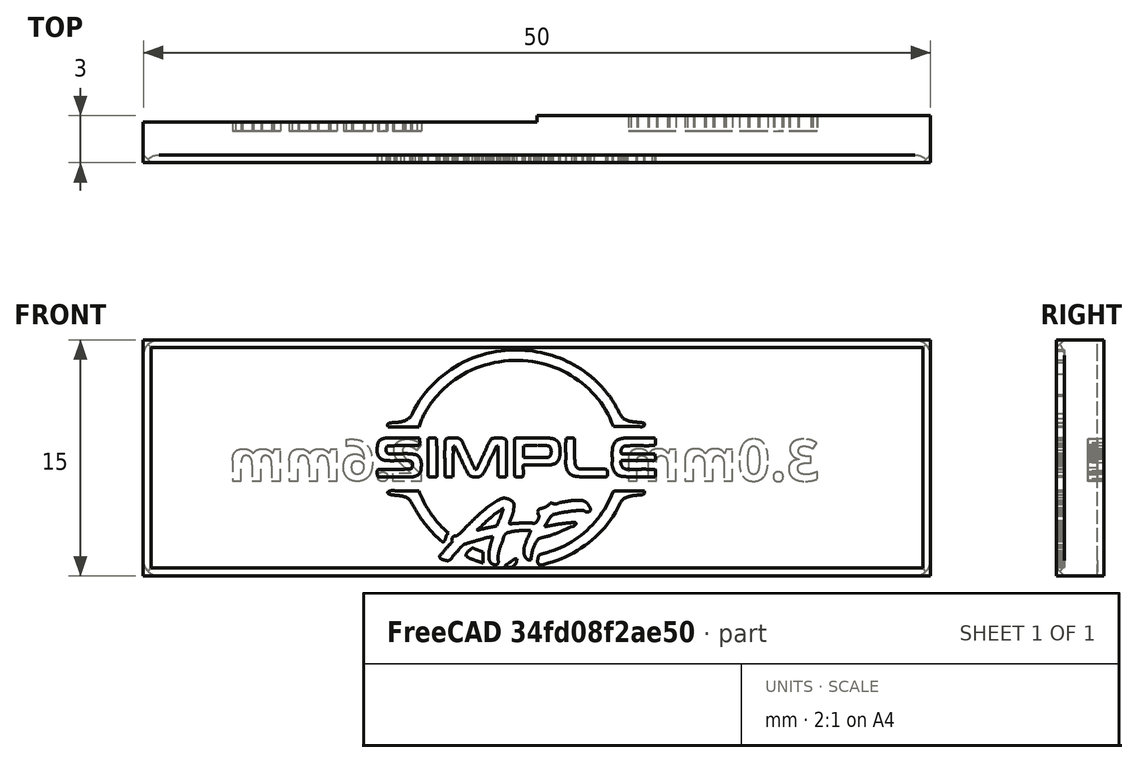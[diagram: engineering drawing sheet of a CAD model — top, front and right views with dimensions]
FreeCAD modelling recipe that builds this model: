
FCSTD DOCUMENT  (FreeCAD 26.3R20260630 (Git shallow))
Label: goldilocks
License: All rights reserved
LicenseURL: http://en.wikipedia.org/wiki/All_rights_reserved
objects: Sketcher::SketchObject×4, App::Point×2, PartDesign::Pad×2, PartDesign::Pocket×2, PartDesign::Body×2, PartDesign::Chamfer×1, PartDesign::Fillet×1
note: 28 computed .brp shape members not serialized (recipe doc carries the construction recipe); baked Part::Feature solids carry a one-line shape summary decoded from their .brp

FEATURE [App::Point] Origin001
  Role = Origin
FEATURE [Sketcher::SketchObject] Sketch
  ArcFitTolerance = 1e-06
  AttachmentSupport = -> [XY_Plane]
  ExternalTypes = [0]
  FullyConstrained = false
  MakeInternals = false
  MapMode = 5
  sketch-geometry (6):
    g0: LineSegment StartX=-28.082 StartY=2.6 StartZ=0 EndX=-3.08196 EndY=2.6 EndZ=0
    g1: LineSegment StartX=-3.08196 StartY=2.6 StartZ=0 EndX=-3.08196 EndY=3 EndZ=0
    g2: LineSegment StartX=-3.08196 StartY=3 StartZ=0 EndX=21.918 EndY=3 EndZ=0
    g3: LineSegment StartX=21.918 StartY=3 StartZ=0 EndX=21.918 EndY=0 EndZ=0
    g4: LineSegment StartX=21.918 StartY=0 StartZ=0 EndX=-28.082 EndY=0 EndZ=0
    g5: LineSegment StartX=-28.082 StartY=0 StartZ=0 EndX=-28.082 EndY=2.6 EndZ=0
  constraints (17):
    c: Horizontal(g0)
    c: Coincident(g0,g1)
    c: Vertical(g1)
    c: Coincident(g1,g2)
    c: Horizontal(g2)
    c: Coincident(g2,g3)
    c: PointOnObject(g3,g-1)
    c: Vertical(g3)
    c: Coincident(g3,g4)
    c: PointOnObject(g4,g-1)
    c: Coincident(g4,g5)
    c: Coincident(g5,g0)
    c: Vertical(g5)
    c: DistanceY(g5,g5) = 2.6
    c: DistanceY(g3,g3) = 3
    c: DistanceX(g4,g4) = 50
    c: DistanceX(g0,g0) = 25
FEATURE [PartDesign::Pad] Pad
  Direction = (0,0,1)
  FuzzyTolerance = 0
  Length = 15
  Length2 = 10
  Profile = -> Sketch
  ReferenceAxis = -> Sketch [N_Axis]
  SideType = 0
  Suppressed = false
  Type = 0
  Type2 = 0
FEATURE [Sketcher::SketchObject] Sketch001
  ArcFitTolerance = 1e-06
  AttachmentOffset = pos=(1,3.5,0) rot=(0,0,1;0rad)
  AttachmentSupport = -> [Pad]
  ExternalTypes = [0]
  FullyConstrained = false
  MakeInternals = true
  MapMode = 5
  Placement = pos=(1,8e-16,3.5) rot=(1,0,0;1.5708rad)
  sketch-geometry (160):
    g0: BSplineCurve PolesCount=4 KnotsCount=2 Degree=3 IsPeriodic=0
    g1: BSplineCurve PolesCount=4 KnotsCount=2 Degree=3 IsPeriodic=0
    g2: BSplineCurve PolesCount=4 KnotsCount=2 Degree=3 IsPeriodic=0
    g3: BSplineCurve PolesCount=4 KnotsCount=2 Degree=3 IsPeriodic=0
    g4: BSplineCurve PolesCount=4 KnotsCount=2 Degree=3 IsPeriodic=0
    g5: BSplineCurve PolesCount=4 KnotsCount=2 Degree=3 IsPeriodic=0
    g6: BSplineCurve PolesCount=4 KnotsCount=2 Degree=3 IsPeriodic=0
    g7: BSplineCurve PolesCount=4 KnotsCount=2 Degree=3 IsPeriodic=0
    g8: BSplineCurve PolesCount=4 KnotsCount=2 Degree=3 IsPeriodic=0
    g9: BSplineCurve PolesCount=4 KnotsCount=2 Degree=3 IsPeriodic=0
    g10: BSplineCurve PolesCount=4 KnotsCount=2 Degree=3 IsPeriodic=0
    g11: BSplineCurve PolesCount=4 KnotsCount=2 Degree=3 IsPeriodic=0
    g12: BSplineCurve PolesCount=4 KnotsCount=2 Degree=3 IsPeriodic=0
    g13: BSplineCurve PolesCount=4 KnotsCount=2 Degree=3 IsPeriodic=0
    g14: BSplineCurve PolesCount=4 KnotsCount=2 Degree=3 IsPeriodic=0
    g15: BSplineCurve PolesCount=4 KnotsCount=2 Degree=3 IsPeriodic=0
    g16: BSplineCurve PolesCount=4 KnotsCount=2 Degree=3 IsPeriodic=0
    g17: BSplineCurve PolesCount=4 KnotsCount=2 Degree=3 IsPeriodic=0
    g18: BSplineCurve PolesCount=4 KnotsCount=2 Degree=3 IsPeriodic=0
    g19: BSplineCurve PolesCount=4 KnotsCount=2 Degree=3 IsPeriodic=0
    g20: BSplineCurve PolesCount=4 KnotsCount=2 Degree=3 IsPeriodic=0
    g21: BSplineCurve PolesCount=4 KnotsCount=2 Degree=3 IsPeriodic=0
    g22: BSplineCurve PolesCount=4 KnotsCount=2 Degree=3 IsPeriodic=0
    g23: BSplineCurve PolesCount=4 KnotsCount=2 Degree=3 IsPeriodic=0
    g24: BSplineCurve PolesCount=4 KnotsCount=2 Degree=3 IsPeriodic=0
    g25: BSplineCurve PolesCount=4 KnotsCount=2 Degree=3 IsPeriodic=0
    g26: BSplineCurve PolesCount=4 KnotsCount=2 Degree=3 IsPeriodic=0
    g27: BSplineCurve PolesCount=4 KnotsCount=2 Degree=3 IsPeriodic=0
    g28: BSplineCurve PolesCount=4 KnotsCount=2 Degree=3 IsPeriodic=0
    g29: BSplineCurve PolesCount=4 KnotsCount=2 Degree=3 IsPeriodic=0
    g30: BSplineCurve PolesCount=4 KnotsCount=2 Degree=3 IsPeriodic=0
    g31: BSplineCurve PolesCount=4 KnotsCount=2 Degree=3 IsPeriodic=0
    g32: BSplineCurve PolesCount=4 KnotsCount=2 Degree=3 IsPeriodic=0
    g33: BSplineCurve PolesCount=4 KnotsCount=2 Degree=3 IsPeriodic=0
    g34: BSplineCurve PolesCount=4 KnotsCount=2 Degree=3 IsPeriodic=0
    g35: BSplineCurve PolesCount=4 KnotsCount=2 Degree=3 IsPeriodic=0
    g36: BSplineCurve PolesCount=4 KnotsCount=2 Degree=3 IsPeriodic=0
    g37: BSplineCurve PolesCount=4 KnotsCount=2 Degree=3 IsPeriodic=0
    g38: BSplineCurve PolesCount=4 KnotsCount=2 Degree=3 IsPeriodic=0
    g39: BSplineCurve PolesCount=4 KnotsCount=2 Degree=3 IsPeriodic=0
    g40: BSplineCurve PolesCount=4 KnotsCount=2 Degree=3 IsPeriodic=0
    g41: BSplineCurve PolesCount=4 KnotsCount=2 Degree=3 IsPeriodic=0
    g42: BSplineCurve PolesCount=4 KnotsCount=2 Degree=3 IsPeriodic=0
    g43: BSplineCurve PolesCount=4 KnotsCount=2 Degree=3 IsPeriodic=0
    g44: BSplineCurve PolesCount=4 KnotsCount=2 Degree=3 IsPeriodic=0
    g45: BSplineCurve PolesCount=4 KnotsCount=2 Degree=3 IsPeriodic=0
    g46: BSplineCurve PolesCount=4 KnotsCount=2 Degree=3 IsPeriodic=0
    g47: BSplineCurve PolesCount=4 KnotsCount=2 Degree=3 IsPeriodic=0
    g48: BSplineCurve PolesCount=4 KnotsCount=2 Degree=3 IsPeriodic=0
    g49: BSplineCurve PolesCount=4 KnotsCount=2 Degree=3 IsPeriodic=0
    g50: BSplineCurve PolesCount=4 KnotsCount=2 Degree=3 IsPeriodic=0
    g51: BSplineCurve PolesCount=4 KnotsCount=2 Degree=3 IsPeriodic=0
    g52: BSplineCurve PolesCount=4 KnotsCount=2 Degree=3 IsPeriodic=0
    g53: BSplineCurve PolesCount=4 KnotsCount=2 Degree=3 IsPeriodic=0
    g54: BSplineCurve PolesCount=4 KnotsCount=2 Degree=3 IsPeriodic=0
    g55: BSplineCurve PolesCount=4 KnotsCount=2 Degree=3 IsPeriodic=0
    g56: BSplineCurve PolesCount=4 KnotsCount=2 Degree=3 IsPeriodic=0
    g57: BSplineCurve PolesCount=4 KnotsCount=2 Degree=3 IsPeriodic=0
    g58: BSplineCurve PolesCount=4 KnotsCount=2 Degree=3 IsPeriodic=0
    g59: BSplineCurve PolesCount=4 KnotsCount=2 Degree=3 IsPeriodic=0
    g60: BSplineCurve PolesCount=4 KnotsCount=2 Degree=3 IsPeriodic=0
    g61: BSplineCurve PolesCount=4 KnotsCount=2 Degree=3 IsPeriodic=0
    g62: BSplineCurve PolesCount=4 KnotsCount=2 Degree=3 IsPeriodic=0
    g63: BSplineCurve PolesCount=4 KnotsCount=2 Degree=3 IsPeriodic=0
    g64: BSplineCurve PolesCount=4 KnotsCount=2 Degree=3 IsPeriodic=0
    g65: BSplineCurve PolesCount=4 KnotsCount=2 Degree=3 IsPeriodic=0
    g66: BSplineCurve PolesCount=4 KnotsCount=2 Degree=3 IsPeriodic=0
    g67: BSplineCurve PolesCount=4 KnotsCount=2 Degree=3 IsPeriodic=0
    g68: BSplineCurve PolesCount=4 KnotsCount=2 Degree=3 IsPeriodic=0
    g69: BSplineCurve PolesCount=4 KnotsCount=2 Degree=3 IsPeriodic=0
    g70: BSplineCurve PolesCount=4 KnotsCount=2 Degree=3 IsPeriodic=0
    g71: BSplineCurve PolesCount=4 KnotsCount=2 Degree=3 IsPeriodic=0
    g72: BSplineCurve PolesCount=4 KnotsCount=2 Degree=3 IsPeriodic=0
    g73: BSplineCurve PolesCount=4 KnotsCount=2 Degree=3 IsPeriodic=0
    g74: BSplineCurve PolesCount=4 KnotsCount=2 Degree=3 IsPeriodic=0
    g75: BSplineCurve PolesCount=4 KnotsCount=2 Degree=3 IsPeriodic=0
    g76: BSplineCurve PolesCount=4 KnotsCount=2 Degree=3 IsPeriodic=0
    g77: BSplineCurve PolesCount=4 KnotsCount=2 Degree=3 IsPeriodic=0
    g78: BSplineCurve PolesCount=4 KnotsCount=2 Degree=3 IsPeriodic=0
    g79: BSplineCurve PolesCount=4 KnotsCount=2 Degree=3 IsPeriodic=0
    g80: BSplineCurve PolesCount=4 KnotsCount=2 Degree=3 IsPeriodic=0
    g81: BSplineCurve PolesCount=4 KnotsCount=2 Degree=3 IsPeriodic=0
    g82: BSplineCurve PolesCount=4 KnotsCount=2 Degree=3 IsPeriodic=0
    g83: BSplineCurve PolesCount=4 KnotsCount=2 Degree=3 IsPeriodic=0
    g84: BSplineCurve PolesCount=4 KnotsCount=2 Degree=3 IsPeriodic=0
    g85: BSplineCurve PolesCount=4 KnotsCount=2 Degree=3 IsPeriodic=0
    g86: BSplineCurve PolesCount=4 KnotsCount=2 Degree=3 IsPeriodic=0
    g87: BSplineCurve PolesCount=4 KnotsCount=2 Degree=3 IsPeriodic=0
    g88: BSplineCurve PolesCount=4 KnotsCount=2 Degree=3 IsPeriodic=0
    g89: BSplineCurve PolesCount=4 KnotsCount=2 Degree=3 IsPeriodic=0
    g90: BSplineCurve PolesCount=4 KnotsCount=2 Degree=3 IsPeriodic=0
    g91: BSplineCurve PolesCount=4 KnotsCount=2 Degree=3 IsPeriodic=0
    g92: BSplineCurve PolesCount=4 KnotsCount=2 Degree=3 IsPeriodic=0
    g93: BSplineCurve PolesCount=4 KnotsCount=2 Degree=3 IsPeriodic=0
    g94: BSplineCurve PolesCount=4 KnotsCount=2 Degree=3 IsPeriodic=0
    g95: BSplineCurve PolesCount=4 KnotsCount=2 Degree=3 IsPeriodic=0
    g96: BSplineCurve PolesCount=4 KnotsCount=2 Degree=3 IsPeriodic=0
    g97: BSplineCurve PolesCount=4 KnotsCount=2 Degree=3 IsPeriodic=0
    g98: BSplineCurve PolesCount=4 KnotsCount=2 Degree=3 IsPeriodic=0
    g99: BSplineCurve PolesCount=4 KnotsCount=2 Degree=3 IsPeriodic=0
    g100: BSplineCurve PolesCount=4 KnotsCount=2 Degree=3 IsPeriodic=0
    g101: BSplineCurve PolesCount=4 KnotsCount=2 Degree=3 IsPeriodic=0
    g102: BSplineCurve PolesCount=4 KnotsCount=2 Degree=3 IsPeriodic=0
    g103: BSplineCurve PolesCount=4 KnotsCount=2 Degree=3 IsPeriodic=0
    g104: BSplineCurve PolesCount=4 KnotsCount=2 Degree=3 IsPeriodic=0
    g105: BSplineCurve PolesCount=2 KnotsCount=2 Degree=1 IsPeriodic=0
    g106: BSplineCurve PolesCount=4 KnotsCount=2 Degree=3 IsPeriodic=0
    g107: BSplineCurve PolesCount=4 KnotsCount=2 Degree=3 IsPeriodic=0
    g108: BSplineCurve PolesCount=4 KnotsCount=2 Degree=3 IsPeriodic=0
    g109: BSplineCurve PolesCount=4 KnotsCount=2 Degree=3 IsPeriodic=0
    g110: BSplineCurve PolesCount=4 KnotsCount=2 Degree=3 IsPeriodic=0
    g111: BSplineCurve PolesCount=4 KnotsCount=2 Degree=3 IsPeriodic=0
    g112: BSplineCurve PolesCount=4 KnotsCount=2 Degree=3 IsPeriodic=0
    g113: BSplineCurve PolesCount=4 KnotsCount=2 Degree=3 IsPeriodic=0
    g114: BSplineCurve PolesCount=4 KnotsCount=2 Degree=3 IsPeriodic=0
    g115: BSplineCurve PolesCount=4 KnotsCount=2 Degree=3 IsPeriodic=0
    g116: BSplineCurve PolesCount=4 KnotsCount=2 Degree=3 IsPeriodic=0
    g117: BSplineCurve PolesCount=4 KnotsCount=2 Degree=3 IsPeriodic=0
    g118: BSplineCurve PolesCount=4 KnotsCount=2 Degree=3 IsPeriodic=0
    g119: BSplineCurve PolesCount=4 KnotsCount=2 Degree=3 IsPeriodic=0
    g120: BSplineCurve PolesCount=4 KnotsCount=2 Degree=3 IsPeriodic=0
    g121: BSplineCurve PolesCount=4 KnotsCount=2 Degree=3 IsPeriodic=0
    g122: BSplineCurve PolesCount=4 KnotsCount=2 Degree=3 IsPeriodic=0
    g123: BSplineCurve PolesCount=4 KnotsCount=2 Degree=3 IsPeriodic=0
    g124: BSplineCurve PolesCount=4 KnotsCount=2 Degree=3 IsPeriodic=0
    g125: BSplineCurve PolesCount=4 KnotsCount=2 Degree=3 IsPeriodic=0
    g126: BSplineCurve PolesCount=4 KnotsCount=2 Degree=3 IsPeriodic=0
    g127: BSplineCurve PolesCount=4 KnotsCount=2 Degree=3 IsPeriodic=0
    g128: BSplineCurve PolesCount=4 KnotsCount=2 Degree=3 IsPeriodic=0
    g129: BSplineCurve PolesCount=4 KnotsCount=2 Degree=3 IsPeriodic=0
    g130: BSplineCurve PolesCount=4 KnotsCount=2 Degree=3 IsPeriodic=0
    g131: BSplineCurve PolesCount=4 KnotsCount=2 Degree=3 IsPeriodic=0
    g132: BSplineCurve PolesCount=4 KnotsCount=2 Degree=3 IsPeriodic=0
    g133: BSplineCurve PolesCount=4 KnotsCount=2 Degree=3 IsPeriodic=0
    g134: BSplineCurve PolesCount=4 KnotsCount=2 Degree=3 IsPeriodic=0
    g135: BSplineCurve PolesCount=4 KnotsCount=2 Degree=3 IsPeriodic=0
    g136: BSplineCurve PolesCount=4 KnotsCount=2 Degree=3 IsPeriodic=0
    g137: BSplineCurve PolesCount=4 KnotsCount=2 Degree=3 IsPeriodic=0
    g138: BSplineCurve PolesCount=4 KnotsCount=2 Degree=3 IsPeriodic=0
    g139: BSplineCurve PolesCount=4 KnotsCount=2 Degree=3 IsPeriodic=0
    g140: BSplineCurve PolesCount=4 KnotsCount=2 Degree=3 IsPeriodic=0
    g141: BSplineCurve PolesCount=4 KnotsCount=2 Degree=3 IsPeriodic=0
    g142: BSplineCurve PolesCount=4 KnotsCount=2 Degree=3 IsPeriodic=0
    g143: BSplineCurve PolesCount=4 KnotsCount=2 Degree=3 IsPeriodic=0
    g144: BSplineCurve PolesCount=4 KnotsCount=2 Degree=3 IsPeriodic=0
    g145: BSplineCurve PolesCount=4 KnotsCount=2 Degree=3 IsPeriodic=0
    g146: BSplineCurve PolesCount=4 KnotsCount=2 Degree=3 IsPeriodic=0
    g147: BSplineCurve PolesCount=4 KnotsCount=2 Degree=3 IsPeriodic=0
    g148: BSplineCurve PolesCount=4 KnotsCount=2 Degree=3 IsPeriodic=0
    g149: BSplineCurve PolesCount=4 KnotsCount=2 Degree=3 IsPeriodic=0
    g150: BSplineCurve PolesCount=4 KnotsCount=2 Degree=3 IsPeriodic=0
    g151: BSplineCurve PolesCount=4 KnotsCount=2 Degree=3 IsPeriodic=0
    g152: BSplineCurve PolesCount=4 KnotsCount=2 Degree=3 IsPeriodic=0
    g153: BSplineCurve PolesCount=4 KnotsCount=2 Degree=3 IsPeriodic=0
    g154: BSplineCurve PolesCount=4 KnotsCount=2 Degree=3 IsPeriodic=0
    g155: BSplineCurve PolesCount=4 KnotsCount=2 Degree=3 IsPeriodic=0
    g156: BSplineCurve PolesCount=4 KnotsCount=2 Degree=3 IsPeriodic=0
    g157: BSplineCurve PolesCount=4 KnotsCount=2 Degree=3 IsPeriodic=0
    g158: BSplineCurve PolesCount=4 KnotsCount=2 Degree=3 IsPeriodic=0
    g159: BSplineCurve PolesCount=4 KnotsCount=2 Degree=3 IsPeriodic=0
  constraints (160):
    c: Coincident(g117,g118)
    c: Coincident(g118,g119)
    c: Coincident(g108,g109)
    c: Coincident(g107,g108)
    c: Coincident(g112,g113)
    c: Coincident(g7,g8)
    c: Coincident(g156,g157)
    c: Coincident(g113,g114)
    c: Coincident(g8,g9)
    c: Coincident(g157,g158)
    c: Coincident(g109,g110)
    c: Coincident(g116,g117)
    c: Coincident(g106,g107)
    c: Coincident(g155,g156)
    c: Coincident(g119,g120)
    c: Coincident(g106,g120)
    c: Coincident(g9,g10)
    c: Coincident(g114,g115)
    c: Coincident(g158,g159)
    c: Coincident(g6,g7)
    c: Coincident(g111,g112)
    c: Coincident(g110,g111)
    c: Coincident(g115,g116)
    c: Coincident(g102,g103)
    c: Coincident(g101,g102)
    c: Coincident(g101,g105)
    c: Coincident(g154,g155)
    c: Coincident(g103,g104)
    c: Coincident(g104,g105)
    c: Coincident(g5,g6)
    c: Coincident(g61,g62)
    c: Coincident(g153,g154)
    c: Coincident(g94,g95)
    c: Coincident(g95,g96)
    c: Coincident(g62,g63)
    c: Coincident(g153,g159)
    c: Coincident(g93,g94)
    c: Coincident(g60,g61)
    c: Coincident(g92,g93)
    c: Coincident(g91,g92)
    c: Coincident(g63,g64)
    c: Coincident(g59,g60)
    c: Coincident(g96,g97)
    c: Coincident(g64,g65)
    c: Coincident(g65,g66)
    c: Coincident(g143,g144)
    c: Coincident(g97,g98)
    c: Coincident(g58,g59)
    c: Coincident(g90,g91)
    c: Coincident(g141,g144)
    c: Coincident(g98,g99)
    c: Coincident(g125,g126)
    c: Coincident(g121,g126)
    c: Coincident(g99,g100)
    c: Coincident(g89,g90)
    c: Coincident(g141,g142)
    c: Coincident(g82,g100)
    c: Coincident(g142,g143)
    c: Coincident(g66,g67)
    c: Coincident(g124,g125)
    c: Coincident(g69,g70)
    c: Coincident(g68,g69)
    c: Coincident(g82,g83)
    c: Coincident(g67,g68)
    c: Coincident(g88,g89)
    c: Coincident(g123,g124)
    c: Coincident(g121,g122)
    c: Coincident(g87,g88)
    c: Coincident(g86,g87)
    c: Coincident(g70,g71)
    c: Coincident(g57,g58)
    c: Coincident(g71,g72)
    c: Coincident(g10,g11)
    c: Coincident(g31,g72)
    c: Coincident(g122,g123)
    c: Coincident(g83,g84)
    c: Coincident(g84,g85)
    c: Coincident(g85,g86)
    c: Coincident(g27,g28)
    c: Coincident(g28,g29)
    c: Coincident(g31,g32)
    c: Coincident(g53,g54)
    c: Coincident(g56,g57)
    c: Coincident(g54,g55)
    c: Coincident(g52,g53)
    c: Coincident(g55,g56)
    c: Coincident(g78,g79)
    c: Coincident(g77,g78)
    c: Coincident(g27,g30)
    c: Coincident(g29,g30)
    c: Coincident(g76,g77)
    c: Coincident(g75,g76)
    c: Coincident(g128,g129)
    c: Coincident(g127,g128)
    c: Coincident(g33,g34)
    c: Coincident(g34,g35)
    c: Coincident(g79,g80)
    c: Coincident(g32,g33)
    c: Coincident(g35,g36)
    c: Coincident(g51,g52)
    c: Coincident(g127,g131)
    c: Coincident(g4,g5)
    c: Coincident(g36,g37)
    c: Coincident(g145,g152)
    c: Coincident(g50,g51)
    c: Coincident(g74,g75)
    c: Coincident(g151,g152)
    c: Coincident(g49,g50)
    c: Coincident(g41,g42)
    c: Coincident(g129,g130)
    c: Coincident(g130,g131)
    c: Coincident(g145,g146)
    c: Coincident(g48,g49)
    c: Coincident(g42,g43)
    c: Coincident(g80,g81)
    c: Coincident(g37,g38)
    c: Coincident(g73,g81)
    c: Coincident(g73,g74)
    c: Coincident(g47,g48)
    c: Coincident(g135,g136)
    c: Coincident(g136,g137)
    c: Coincident(g38,g39)
    c: Coincident(g39,g40)
    c: Coincident(g40,g41)
    c: Coincident(g134,g135)
    c: Coincident(g137,g138)
    c: Coincident(g138,g139)
    c: Coincident(g46,g47)
    c: Coincident(g43,g44)
    c: Coincident(g11,g12)
    c: Coincident(g45,g46)
    c: Coincident(g44,g45)
    c: Coincident(g139,g140)
    c: Coincident(g132,g140)
    c: Coincident(g133,g134)
    c: Coincident(g132,g133)
    c: Coincident(g0,g12)
    c: Coincident(g24,g25)
    c: Coincident(g146,g147)
    c: Coincident(g3,g4)
    c: Coincident(g25,g26)
    c: Coincident(g150,g151)
    c: Coincident(g19,g20)
    c: Coincident(g16,g17)
    c: Coincident(g23,g24)
    c: Coincident(g0,g1)
    c: Coincident(g15,g16)
    c: Coincident(g13,g26)
    c: Coincident(g147,g148)
    c: Coincident(g20,g21)
    c: Coincident(g2,g3)
    c: Coincident(g149,g150)
    c: Coincident(g1,g2)
    c: Coincident(g148,g149)
    c: Coincident(g18,g19)
    c: Coincident(g22,g23)
    c: Coincident(g14,g15)
    c: Coincident(g17,g18)
    c: Coincident(g21,g22)
    c: Coincident(g13,g14)
FEATURE [PartDesign::Pocket] Pocket
  BaseFeature = -> Pad
  Direction = (0,1,-2e-16)
  FuzzyTolerance = 0
  Length = 0.5
  Length2 = 5
  Profile = -> Sketch001
  ReferenceAxis = -> Sketch001 [N_Axis]
  Refine = true
  SideType = 0
  Suppressed = false
  Type = 0
  Type2 = 0
FEATURE [PartDesign::Chamfer] Chamfer
  Angle = 45
  Base = -> Pocket [Edge13,Edge16,Edge17,Edge5]
  BaseFeature = -> Pocket
  ChamferType = 0
  FlipDirection = false
  FuzzyTolerance = 0
  Refine = true
  Size = 0.5
  Size2 = 1
  SupportTransform = false
  Suppressed = false
  UseAllEdges = false
FEATURE [PartDesign::Fillet] Fillet
  Base = -> Chamfer [Edge5,Edge1,Edge4,Edge15]
  BaseFeature = -> Chamfer
  FuzzyTolerance = 0
  Radius = 1
  Refine = true
  SupportTransform = false
  Suppressed = false
  UseAllEdges = false
FEATURE [Sketcher::SketchObject] Sketch002
  ArcFitTolerance = 1e-06
  AttachmentSupport = -> [Fillet]
  ExternalTypes = [0]
  FullyConstrained = false
  MakeInternals = true
  MapMode = 5
  Placement = pos=(0,3,0) rot=(0,0.707107,0.707107;3.14159rad)
  sketch-geometry (222):
    g0: LineSegment [constr] StartX=-14.7202 StartY=6 StartZ=0 EndX=-2.72016 EndY=6 EndZ=0
    g1: LineSegment [constr] StartX=10.4105 StartY=6 StartZ=0 EndX=22.4105 EndY=6 EndZ=0
    g2: BSplineCurve PolesCount=3 KnotsCount=2 Degree=2 IsPeriodic=0
    g3: BSplineCurve PolesCount=3 KnotsCount=2 Degree=2 IsPeriodic=0
    g4: LineSegment StartX=-13.5529 StartY=7.4247 StartZ=0 EndX=-13.5529 EndY=7.41397 EndZ=0
    g5: BSplineCurve PolesCount=3 KnotsCount=2 Degree=2 IsPeriodic=0
    g6: BSplineCurve PolesCount=3 KnotsCount=2 Degree=2 IsPeriodic=0
    g7: BSplineCurve PolesCount=3 KnotsCount=2 Degree=2 IsPeriodic=0
    g8: BSplineCurve PolesCount=3 KnotsCount=2 Degree=2 IsPeriodic=0
    g9: BSplineCurve PolesCount=3 KnotsCount=2 Degree=2 IsPeriodic=0
    g10: LineSegment StartX=-14.7202 StartY=6.15373 StartZ=0 EndX=-14.7202 EndY=6.62386 EndZ=0
    g11: BSplineCurve PolesCount=3 KnotsCount=2 Degree=2 IsPeriodic=0
    g12: BSplineCurve PolesCount=3 KnotsCount=2 Degree=2 IsPeriodic=0
    g13: BSplineCurve PolesCount=3 KnotsCount=2 Degree=2 IsPeriodic=0
    g14: BSplineCurve PolesCount=3 KnotsCount=2 Degree=2 IsPeriodic=0
    g15: BSplineCurve PolesCount=3 KnotsCount=2 Degree=2 IsPeriodic=0
    g16: BSplineCurve PolesCount=3 KnotsCount=2 Degree=2 IsPeriodic=0
    g17: LineSegment StartX=-14.1195 StartY=7.1798 StartZ=0 EndX=-14.318 EndY=7.1798 EndZ=0
    g18: LineSegment StartX=-14.318 StartY=7.1798 StartZ=0 EndX=-14.318 EndY=7.60346 EndZ=0
    g19: LineSegment StartX=-14.318 StartY=7.60346 StartZ=0 EndX=-14.116 EndY=7.60346 EndZ=0
    g20: BSplineCurve PolesCount=3 KnotsCount=2 Degree=2 IsPeriodic=0
    g21: BSplineCurve PolesCount=3 KnotsCount=2 Degree=2 IsPeriodic=0
    g22: BSplineCurve PolesCount=3 KnotsCount=2 Degree=2 IsPeriodic=0
    g23: BSplineCurve PolesCount=3 KnotsCount=2 Degree=2 IsPeriodic=0
    g24: BSplineCurve PolesCount=3 KnotsCount=2 Degree=2 IsPeriodic=0
    g25: LineSegment StartX=-14.461 StartY=8.06108 StartZ=0 EndX=-14.7166 EndY=8.44183 EndZ=0
    g26: BSplineCurve PolesCount=3 KnotsCount=2 Degree=2 IsPeriodic=0
    g27: BSplineCurve PolesCount=3 KnotsCount=2 Degree=2 IsPeriodic=0
    g28: BSplineCurve PolesCount=3 KnotsCount=2 Degree=2 IsPeriodic=0
    g29: BSplineCurve PolesCount=3 KnotsCount=2 Degree=2 IsPeriodic=0
    g30: BSplineCurve PolesCount=3 KnotsCount=2 Degree=2 IsPeriodic=0
    g31: BSplineCurve PolesCount=3 KnotsCount=2 Degree=2 IsPeriodic=0
    g32: BSplineCurve PolesCount=3 KnotsCount=2 Degree=2 IsPeriodic=0
    g33: BSplineCurve PolesCount=3 KnotsCount=2 Degree=2 IsPeriodic=0
    g34: BSplineCurve PolesCount=3 KnotsCount=2 Degree=2 IsPeriodic=0
    g35: BSplineCurve PolesCount=3 KnotsCount=2 Degree=2 IsPeriodic=0
    g36: BSplineCurve PolesCount=3 KnotsCount=2 Degree=2 IsPeriodic=0
    g37: BSplineCurve PolesCount=3 KnotsCount=2 Degree=2 IsPeriodic=0
    g38: BSplineCurve PolesCount=3 KnotsCount=2 Degree=2 IsPeriodic=0
    g39: BSplineCurve PolesCount=3 KnotsCount=2 Degree=2 IsPeriodic=0
    g40: BSplineCurve PolesCount=3 KnotsCount=2 Degree=2 IsPeriodic=0
    g41: BSplineCurve PolesCount=3 KnotsCount=2 Degree=2 IsPeriodic=0
    g42: BSplineCurve PolesCount=3 KnotsCount=2 Degree=2 IsPeriodic=0
    g43: BSplineCurve PolesCount=3 KnotsCount=2 Degree=2 IsPeriodic=0
    g44: BSplineCurve PolesCount=3 KnotsCount=2 Degree=2 IsPeriodic=0
    g45: BSplineCurve PolesCount=3 KnotsCount=2 Degree=2 IsPeriodic=0
    g46: BSplineCurve PolesCount=3 KnotsCount=2 Degree=2 IsPeriodic=0
    g47: BSplineCurve PolesCount=3 KnotsCount=2 Degree=2 IsPeriodic=0
    g48: BSplineCurve PolesCount=3 KnotsCount=2 Degree=2 IsPeriodic=0
    g49: BSplineCurve PolesCount=3 KnotsCount=2 Degree=2 IsPeriodic=0
    g50: BSplineCurve PolesCount=3 KnotsCount=2 Degree=2 IsPeriodic=0
    g51: BSplineCurve PolesCount=3 KnotsCount=2 Degree=2 IsPeriodic=0
    g52: BSplineCurve PolesCount=3 KnotsCount=2 Degree=2 IsPeriodic=0
    g53: LineSegment StartX=-7.56092 StartY=6.04826 StartZ=0 EndX=-8.10613 EndY=6.04826 EndZ=0
    g54: LineSegment StartX=-8.10613 StartY=6.04826 StartZ=0 EndX=-8.10613 EndY=7.21555 EndZ=0
    g55: BSplineCurve PolesCount=3 KnotsCount=2 Degree=2 IsPeriodic=0
    g56: BSplineCurve PolesCount=3 KnotsCount=2 Degree=2 IsPeriodic=0
    g57: BSplineCurve PolesCount=3 KnotsCount=2 Degree=2 IsPeriodic=0
    g58: BSplineCurve PolesCount=3 KnotsCount=2 Degree=2 IsPeriodic=0
    g59: LineSegment StartX=-8.80507 StartY=6.98853 StartZ=0 EndX=-8.80507 EndY=6.04826 EndZ=0
    g60: LineSegment StartX=-8.80507 StartY=6.04826 StartZ=0 EndX=-9.35028 EndY=6.04826 EndZ=0
    g61: LineSegment StartX=-9.35028 StartY=6.04826 StartZ=0 EndX=-9.35028 EndY=8.04678 EndZ=0
    g62: LineSegment StartX=-9.35028 StartY=8.04678 StartZ=0 EndX=-8.93378 EndY=8.04678 EndZ=0
    g63: LineSegment StartX=-8.93378 StartY=8.04678 StartZ=0 EndX=-8.86048 EndY=7.79115 EndZ=0
    g64: LineSegment StartX=-8.86048 StartY=7.79115 StartZ=0 EndX=-8.8301 EndY=7.79115 EndZ=0
    g65: BSplineCurve PolesCount=3 KnotsCount=2 Degree=2 IsPeriodic=0
    g66: BSplineCurve PolesCount=3 KnotsCount=2 Degree=2 IsPeriodic=0
    g67: BSplineCurve PolesCount=3 KnotsCount=2 Degree=2 IsPeriodic=0
    g68: LineSegment StartX=-7.64136 StartY=7.79115 StartZ=0 EndX=-7.59309 EndY=7.79115 EndZ=0
    g69: BSplineCurve PolesCount=3 KnotsCount=2 Degree=2 IsPeriodic=0
    g70: BSplineCurve PolesCount=3 KnotsCount=2 Degree=2 IsPeriodic=0
    g71: BSplineCurve PolesCount=3 KnotsCount=2 Degree=2 IsPeriodic=0
    g72: BSplineCurve PolesCount=3 KnotsCount=2 Degree=2 IsPeriodic=0
    g73: LineSegment StartX=-6.31498 StartY=7.35141 StartZ=0 EndX=-6.31498 EndY=6.04826 EndZ=0
    g74: LineSegment StartX=-6.31498 StartY=6.04826 StartZ=0 EndX=-6.86197 EndY=6.04826 EndZ=0
    g75: LineSegment StartX=-6.86197 StartY=6.04826 StartZ=0 EndX=-6.86197 EndY=7.21555 EndZ=0
    g76: BSplineCurve PolesCount=3 KnotsCount=2 Degree=2 IsPeriodic=0
    g77: BSplineCurve PolesCount=3 KnotsCount=2 Degree=2 IsPeriodic=0
    g78: BSplineCurve PolesCount=3 KnotsCount=2 Degree=2 IsPeriodic=0
    g79: BSplineCurve PolesCount=3 KnotsCount=2 Degree=2 IsPeriodic=0
    g80: LineSegment StartX=-7.56092 StartY=7.0511 StartZ=0 EndX=-7.56092 EndY=6.04826 EndZ=0
    g81: LineSegment StartX=-3.9661 StartY=6.04826 StartZ=0 EndX=-4.51131 EndY=6.04826 EndZ=0
    g82: LineSegment StartX=-4.51131 StartY=6.04826 StartZ=0 EndX=-4.51131 EndY=7.21555 EndZ=0
    g83: BSplineCurve PolesCount=3 KnotsCount=2 Degree=2 IsPeriodic=0
    g84: BSplineCurve PolesCount=3 KnotsCount=2 Degree=2 IsPeriodic=0
    g85: BSplineCurve PolesCount=3 KnotsCount=2 Degree=2 IsPeriodic=0
    g86: BSplineCurve PolesCount=3 KnotsCount=2 Degree=2 IsPeriodic=0
    g87: LineSegment StartX=-5.21025 StartY=6.98853 StartZ=0 EndX=-5.21025 EndY=6.04826 EndZ=0
    g88: LineSegment StartX=-5.21025 StartY=6.04826 StartZ=0 EndX=-5.75546 EndY=6.04826 EndZ=0
    g89: LineSegment StartX=-5.75546 StartY=6.04826 StartZ=0 EndX=-5.75546 EndY=8.04678 EndZ=0
    g90: LineSegment StartX=-5.75546 StartY=8.04678 StartZ=0 EndX=-5.33896 EndY=8.04678 EndZ=0
    g91: LineSegment StartX=-5.33896 StartY=8.04678 StartZ=0 EndX=-5.26567 EndY=7.79115 EndZ=0
    g92: LineSegment StartX=-5.26567 StartY=7.79115 StartZ=0 EndX=-5.23528 EndY=7.79115 EndZ=0
    g93: BSplineCurve PolesCount=3 KnotsCount=2 Degree=2 IsPeriodic=0
    g94: BSplineCurve PolesCount=3 KnotsCount=2 Degree=2 IsPeriodic=0
    g95: BSplineCurve PolesCount=3 KnotsCount=2 Degree=2 IsPeriodic=0
    g96: LineSegment StartX=-4.04654 StartY=7.79115 StartZ=0 EndX=-3.99828 EndY=7.79115 EndZ=0
    g97: BSplineCurve PolesCount=3 KnotsCount=2 Degree=2 IsPeriodic=0
    g98: BSplineCurve PolesCount=3 KnotsCount=2 Degree=2 IsPeriodic=0
    g99: BSplineCurve PolesCount=3 KnotsCount=2 Degree=2 IsPeriodic=0
    g100: BSplineCurve PolesCount=3 KnotsCount=2 Degree=2 IsPeriodic=0
    g101: LineSegment StartX=-2.72016 StartY=7.35141 StartZ=0 EndX=-2.72016 EndY=6.04826 EndZ=0
    g102: LineSegment StartX=-2.72016 StartY=6.04826 StartZ=0 EndX=-3.26716 EndY=6.04826 EndZ=0
    g103: LineSegment StartX=-3.26716 StartY=6.04826 StartZ=0 EndX=-3.26716 EndY=7.21555 EndZ=0
    g104: BSplineCurve PolesCount=3 KnotsCount=2 Degree=2 IsPeriodic=0
    g105: BSplineCurve PolesCount=3 KnotsCount=2 Degree=2 IsPeriodic=0
    g106: BSplineCurve PolesCount=3 KnotsCount=2 Degree=2 IsPeriodic=0
    g107: BSplineCurve PolesCount=3 KnotsCount=2 Degree=2 IsPeriodic=0
    g108: LineSegment StartX=-3.9661 StartY=7.0511 StartZ=0 EndX=-3.9661 EndY=6.04826 EndZ=0
    g109: LineSegment StartX=12.2446 StartY=6.04826 StartZ=0 EndX=10.4177 EndY=6.04826 EndZ=0
    g110: LineSegment StartX=10.4177 StartY=6.04826 StartZ=0 EndX=10.4177 EndY=6.43259 EndZ=0
    g111: LineSegment StartX=10.4177 StartY=6.43259 StartZ=0 EndX=11.0737 EndY=7.09578 EndZ=0
    g112: BSplineCurve PolesCount=3 KnotsCount=2 Degree=2 IsPeriodic=0
    g113: BSplineCurve PolesCount=3 KnotsCount=2 Degree=2 IsPeriodic=0
    g114: BSplineCurve PolesCount=3 KnotsCount=2 Degree=2 IsPeriodic=0
    g115: BSplineCurve PolesCount=3 KnotsCount=2 Degree=2 IsPeriodic=0
    g116: BSplineCurve PolesCount=3 KnotsCount=2 Degree=2 IsPeriodic=0
    g117: BSplineCurve PolesCount=3 KnotsCount=2 Degree=2 IsPeriodic=0
    g118: BSplineCurve PolesCount=3 KnotsCount=2 Degree=2 IsPeriodic=0
    g119: LineSegment StartX=10.7108 StartY=7.96991 StartZ=0 EndX=10.4105 EndY=8.32564 EndZ=0
    g120: BSplineCurve PolesCount=3 KnotsCount=2 Degree=2 IsPeriodic=0
    g121: BSplineCurve PolesCount=3 KnotsCount=2 Degree=2 IsPeriodic=0
    g122: BSplineCurve PolesCount=3 KnotsCount=2 Degree=2 IsPeriodic=0
    g123: BSplineCurve PolesCount=3 KnotsCount=2 Degree=2 IsPeriodic=0
    g124: BSplineCurve PolesCount=3 KnotsCount=2 Degree=2 IsPeriodic=0
    g125: BSplineCurve PolesCount=3 KnotsCount=2 Degree=2 IsPeriodic=0
    g126: BSplineCurve PolesCount=3 KnotsCount=2 Degree=2 IsPeriodic=0
    g127: BSplineCurve PolesCount=3 KnotsCount=2 Degree=2 IsPeriodic=0
    g128: BSplineCurve PolesCount=3 KnotsCount=2 Degree=2 IsPeriodic=0
    g129: LineSegment StartX=11.4419 StartY=6.85446 StartZ=0 EndX=11.1059 EndY=6.53806 EndZ=0
    g130: LineSegment StartX=11.1059 StartY=6.53806 StartZ=0 EndX=11.1059 EndY=6.51303 EndZ=0
    g131: LineSegment StartX=11.1059 StartY=6.51303 StartZ=0 EndX=12.2446 EndY=6.51303 EndZ=0
    g132: LineSegment StartX=12.2446 StartY=6.51303 StartZ=0 EndX=12.2446 EndY=6.04826 EndZ=0
    g133: BSplineCurve PolesCount=3 KnotsCount=2 Degree=2 IsPeriodic=0
    g134: BSplineCurve PolesCount=3 KnotsCount=2 Degree=2 IsPeriodic=0
    g135: BSplineCurve PolesCount=3 KnotsCount=2 Degree=2 IsPeriodic=0
    g136: BSplineCurve PolesCount=3 KnotsCount=2 Degree=2 IsPeriodic=0
    g137: BSplineCurve PolesCount=3 KnotsCount=2 Degree=2 IsPeriodic=0
    g138: BSplineCurve PolesCount=3 KnotsCount=2 Degree=2 IsPeriodic=0
    g139: BSplineCurve PolesCount=3 KnotsCount=2 Degree=2 IsPeriodic=0
    g140: BSplineCurve PolesCount=3 KnotsCount=2 Degree=2 IsPeriodic=0
    g141: BSplineCurve PolesCount=3 KnotsCount=2 Degree=2 IsPeriodic=0
    g142: BSplineCurve PolesCount=3 KnotsCount=2 Degree=2 IsPeriodic=0
    g143: BSplineCurve PolesCount=3 KnotsCount=2 Degree=2 IsPeriodic=0
    g144: LineSegment StartX=15.1941 StartY=8.66528 StartZ=0 EndX=15.1941 EndY=8.22375 EndZ=0
    g145: BSplineCurve PolesCount=3 KnotsCount=2 Degree=2 IsPeriodic=0
    g146: BSplineCurve PolesCount=3 KnotsCount=2 Degree=2 IsPeriodic=0
    g147: BSplineCurve PolesCount=3 KnotsCount=2 Degree=2 IsPeriodic=0
    g148: BSplineCurve PolesCount=3 KnotsCount=2 Degree=2 IsPeriodic=0
    g149: LineSegment StartX=14.0411 StartY=7.44257 StartZ=0 EndX=14.0643 EndY=7.44257 EndZ=0
    g150: BSplineCurve PolesCount=3 KnotsCount=2 Degree=2 IsPeriodic=0
    g151: BSplineCurve PolesCount=3 KnotsCount=2 Degree=2 IsPeriodic=0
    g152: BSplineCurve PolesCount=3 KnotsCount=2 Degree=2 IsPeriodic=0
    g153: BSplineCurve PolesCount=3 KnotsCount=2 Degree=2 IsPeriodic=0
    g154: BSplineCurve PolesCount=3 KnotsCount=2 Degree=2 IsPeriodic=0
    g155: BSplineCurve PolesCount=3 KnotsCount=2 Degree=2 IsPeriodic=0
    g156: BSplineCurve PolesCount=3 KnotsCount=2 Degree=2 IsPeriodic=0
    g157: BSplineCurve PolesCount=3 KnotsCount=2 Degree=2 IsPeriodic=0
    g158: BSplineCurve PolesCount=3 KnotsCount=2 Degree=2 IsPeriodic=0
    g159: BSplineCurve PolesCount=3 KnotsCount=2 Degree=2 IsPeriodic=0
    g160: BSplineCurve PolesCount=3 KnotsCount=2 Degree=2 IsPeriodic=0
    g161: BSplineCurve PolesCount=3 KnotsCount=2 Degree=2 IsPeriodic=0
    g162: BSplineCurve PolesCount=3 KnotsCount=2 Degree=2 IsPeriodic=0
    g163: BSplineCurve PolesCount=3 KnotsCount=2 Degree=2 IsPeriodic=0
    g164: BSplineCurve PolesCount=3 KnotsCount=2 Degree=2 IsPeriodic=0
    g165: BSplineCurve PolesCount=3 KnotsCount=2 Degree=2 IsPeriodic=0
    g166: LineSegment StartX=17.5697 StartY=6.04826 StartZ=0 EndX=17.0245 EndY=6.04826 EndZ=0
    g167: LineSegment StartX=17.0245 StartY=6.04826 StartZ=0 EndX=17.0245 EndY=7.21555 EndZ=0
    g168: BSplineCurve PolesCount=3 KnotsCount=2 Degree=2 IsPeriodic=0
    g169: BSplineCurve PolesCount=3 KnotsCount=2 Degree=2 IsPeriodic=0
    g170: BSplineCurve PolesCount=3 KnotsCount=2 Degree=2 IsPeriodic=0
    g171: BSplineCurve PolesCount=3 KnotsCount=2 Degree=2 IsPeriodic=0
    g172: LineSegment StartX=16.3256 StartY=6.98853 StartZ=0 EndX=16.3256 EndY=6.04826 EndZ=0
    g173: LineSegment StartX=16.3256 StartY=6.04826 StartZ=0 EndX=15.7804 EndY=6.04826 EndZ=0
    g174: LineSegment StartX=15.7804 StartY=6.04826 StartZ=0 EndX=15.7804 EndY=8.04678 EndZ=0
    g175: LineSegment StartX=15.7804 StartY=8.04678 StartZ=0 EndX=16.1969 EndY=8.04678 EndZ=0
    g176: LineSegment StartX=16.1969 StartY=8.04678 StartZ=0 EndX=16.2702 EndY=7.79115 EndZ=0
    g177: LineSegment StartX=16.2702 StartY=7.79115 StartZ=0 EndX=16.3006 EndY=7.79115 EndZ=0
    g178: BSplineCurve PolesCount=3 KnotsCount=2 Degree=2 IsPeriodic=0
    g179: BSplineCurve PolesCount=3 KnotsCount=2 Degree=2 IsPeriodic=0
    g180: BSplineCurve PolesCount=3 KnotsCount=2 Degree=2 IsPeriodic=0
    g181: LineSegment StartX=17.4893 StartY=7.79115 StartZ=0 EndX=17.5376 EndY=7.79115 EndZ=0
    g182: BSplineCurve PolesCount=3 KnotsCount=2 Degree=2 IsPeriodic=0
    g183: BSplineCurve PolesCount=3 KnotsCount=2 Degree=2 IsPeriodic=0
    g184: BSplineCurve PolesCount=3 KnotsCount=2 Degree=2 IsPeriodic=0
    g185: BSplineCurve PolesCount=3 KnotsCount=2 Degree=2 IsPeriodic=0
    g186: LineSegment StartX=18.8157 StartY=7.35141 StartZ=0 EndX=18.8157 EndY=6.04826 EndZ=0
    g187: LineSegment StartX=18.8157 StartY=6.04826 StartZ=0 EndX=18.2687 EndY=6.04826 EndZ=0
    g188: LineSegment StartX=18.2687 StartY=6.04826 StartZ=0 EndX=18.2687 EndY=7.21555 EndZ=0
    g189: BSplineCurve PolesCount=3 KnotsCount=2 Degree=2 IsPeriodic=0
    g190: BSplineCurve PolesCount=3 KnotsCount=2 Degree=2 IsPeriodic=0
    g191: BSplineCurve PolesCount=3 KnotsCount=2 Degree=2 IsPeriodic=0
    g192: BSplineCurve PolesCount=3 KnotsCount=2 Degree=2 IsPeriodic=0
    g193: LineSegment StartX=17.5697 StartY=7.0511 StartZ=0 EndX=17.5697 EndY=6.04826 EndZ=0
    g194: LineSegment StartX=21.1646 StartY=6.04826 StartZ=0 EndX=20.6193 EndY=6.04826 EndZ=0
    g195: LineSegment StartX=20.6193 StartY=6.04826 StartZ=0 EndX=20.6193 EndY=7.21555 EndZ=0
    g196: BSplineCurve PolesCount=3 KnotsCount=2 Degree=2 IsPeriodic=0
    g197: BSplineCurve PolesCount=3 KnotsCount=2 Degree=2 IsPeriodic=0
    g198: BSplineCurve PolesCount=3 KnotsCount=2 Degree=2 IsPeriodic=0
    g199: BSplineCurve PolesCount=3 KnotsCount=2 Degree=2 IsPeriodic=0
    g200: LineSegment StartX=19.9204 StartY=6.98853 StartZ=0 EndX=19.9204 EndY=6.04826 EndZ=0
    g201: LineSegment StartX=19.9204 StartY=6.04826 StartZ=0 EndX=19.3752 EndY=6.04826 EndZ=0
    g202: LineSegment StartX=19.3752 StartY=6.04826 StartZ=0 EndX=19.3752 EndY=8.04678 EndZ=0
    g203: LineSegment StartX=19.3752 StartY=8.04678 StartZ=0 EndX=19.7917 EndY=8.04678 EndZ=0
    g204: LineSegment StartX=19.7917 StartY=8.04678 StartZ=0 EndX=19.865 EndY=7.79115 EndZ=0
    g205: LineSegment StartX=19.865 StartY=7.79115 StartZ=0 EndX=19.8954 EndY=7.79115 EndZ=0
    g206: BSplineCurve PolesCount=3 KnotsCount=2 Degree=2 IsPeriodic=0
    g207: BSplineCurve PolesCount=3 KnotsCount=2 Degree=2 IsPeriodic=0
    g208: BSplineCurve PolesCount=3 KnotsCount=2 Degree=2 IsPeriodic=0
    g209: LineSegment StartX=21.0841 StartY=7.79115 StartZ=0 EndX=21.1324 EndY=7.79115 EndZ=0
    g210: BSplineCurve PolesCount=3 KnotsCount=2 Degree=2 IsPeriodic=0
    g211: BSplineCurve PolesCount=3 KnotsCount=2 Degree=2 IsPeriodic=0
    g212: BSplineCurve PolesCount=3 KnotsCount=2 Degree=2 IsPeriodic=0
    g213: BSplineCurve PolesCount=3 KnotsCount=2 Degree=2 IsPeriodic=0
    g214: LineSegment StartX=22.4105 StartY=7.35141 StartZ=0 EndX=22.4105 EndY=6.04826 EndZ=0
    g215: LineSegment StartX=22.4105 StartY=6.04826 StartZ=0 EndX=21.8635 EndY=6.04826 EndZ=0
    g216: LineSegment StartX=21.8635 StartY=6.04826 StartZ=0 EndX=21.8635 EndY=7.21555 EndZ=0
    g217: BSplineCurve PolesCount=3 KnotsCount=2 Degree=2 IsPeriodic=0
    g218: BSplineCurve PolesCount=3 KnotsCount=2 Degree=2 IsPeriodic=0
    g219: BSplineCurve PolesCount=3 KnotsCount=2 Degree=2 IsPeriodic=0
    g220: BSplineCurve PolesCount=3 KnotsCount=2 Degree=2 IsPeriodic=0
    g221: LineSegment StartX=21.1646 StartY=7.0511 StartZ=0 EndX=21.1646 EndY=6.04826 EndZ=0
  constraints (9):
    c: Horizontal(g0)
    c: Horizontal(g1)
    c: DistanceX(g1,g1) = 12
    c: DistanceX(g0,g0) = 12
    c: DistanceY(g-1,g-3) = 15
    c: DistanceY(g0,g-3) = 9
    c: DistanceY(g1,g-3) = 9
    c: T21(g0,g2,g3)
    c: T21(g1,g109,g110)
FEATURE [PartDesign::Pocket] Pocket001
  BaseFeature = -> Fillet
  Direction = (0,-1,2e-16)
  FuzzyTolerance = 0
  Length = 1
  Length2 = 5
  Profile = -> Sketch002
  ReferenceAxis = -> Sketch002 [N_Axis]
  Refine = true
  SideType = 0
  Suppressed = false
  Type = 0
  Type2 = 0
FEATURE [PartDesign::Body] Body  label="Goldilocks"
  AllowCompound = false
  Group = -> [Sketch,Pad,Sketch001,Pocket,Chamfer,Fillet,Sketch002,Pocket001]
  Origin = -> Origin
  Tip = -> Pocket001
FEATURE [App::Point] Origin003
  Role = Origin
FEATURE [Sketcher::SketchObject] Sketch003
  ArcFitTolerance = 1e-06
  AttachmentSupport = -> [XY_Plane001]
  ExternalTypes = [0]
  FullyConstrained = false
  MakeInternals = false
  MapMode = 5
  sketch-geometry (6):
    g0: LineSegment StartX=-28.082 StartY=2.6 StartZ=0 EndX=-3.08196 EndY=2.6 EndZ=0
    g1: LineSegment StartX=-3.08196 StartY=2.6 StartZ=0 EndX=-3.08196 EndY=3 EndZ=0
    g2: LineSegment StartX=-3.08196 StartY=3 StartZ=0 EndX=21.918 EndY=3 EndZ=0
    g3: LineSegment StartX=21.918 StartY=3 StartZ=0 EndX=21.918 EndY=0 EndZ=0
    g4: LineSegment StartX=21.918 StartY=0 StartZ=0 EndX=-28.082 EndY=0 EndZ=0
    g5: LineSegment StartX=-28.082 StartY=0 StartZ=0 EndX=-28.082 EndY=2.6 EndZ=0
  constraints (17):
    c: Horizontal(g0)
    c: Coincident(g0,g1)
    c: Vertical(g1)
    c: Coincident(g1,g2)
    c: Horizontal(g2)
    c: Coincident(g2,g3)
    c: PointOnObject(g3,g-1)
    c: Vertical(g3)
    c: Coincident(g3,g4)
    c: PointOnObject(g4,g-1)
    c: Coincident(g4,g5)
    c: Coincident(g5,g0)
    c: Vertical(g5)
    c: DistanceY(g5,g5) = 2.6
    c: DistanceY(g3,g3) = 3
    c: DistanceX(g4,g4) = 50
    c: DistanceX(g0,g0) = 25
FEATURE [PartDesign::Pad] Pad001
  Direction = (0,0,1)
  FuzzyTolerance = 0
  Length = 15
  Length2 = 10
  Profile = -> Sketch003
  ReferenceAxis = -> Sketch003 [N_Axis]
  SideType = 0
  Suppressed = false
  Type = 0
  Type2 = 0
FEATURE [PartDesign::Body] Body001  label="Goldilocks-Plain"
  AllowCompound = false
  Group = -> [Sketch003,Pad001]
  Origin = -> Origin002
  Tip = -> Pad001
